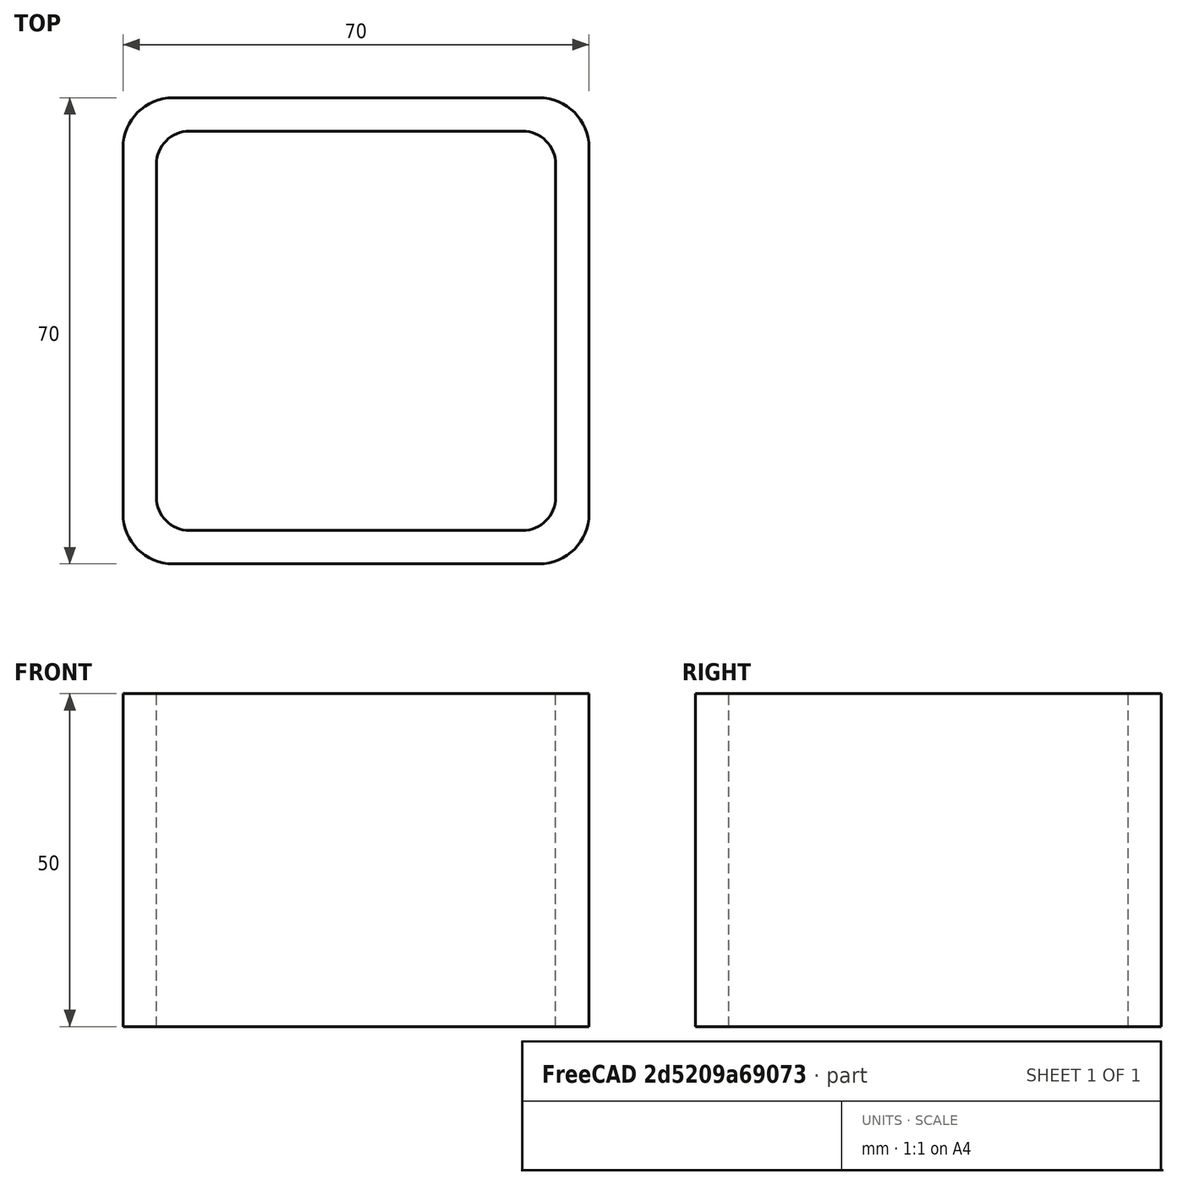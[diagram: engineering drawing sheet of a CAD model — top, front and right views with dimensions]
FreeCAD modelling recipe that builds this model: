
FCSTD DOCUMENT  (FreeCAD 0.15R4671 (Git))
Label: Square hollow section 70x70x5 EN10219 S235JRH
License: All rights reserved
LicenseURL: http://en.wikipedia.org/wiki/All_rights_reserved
objects: Sketcher::SketchObject×1, Part::Extrusion×1
note: 2 computed .brp shape members not serialized (recipe doc carries the construction recipe); baked Part::Feature solids carry a one-line shape summary decoded from their .brp

FEATURE [Sketcher::SketchObject] Sketch
  sketch-geometry (16):
    g0: LineSegment StartX=-25 StartY=30 StartZ=0 EndX=25 EndY=30 EndZ=0
    g1: LineSegment StartX=30 StartY=25 StartZ=0 EndX=30 EndY=-25 EndZ=0
    g2: LineSegment StartX=25 StartY=-30 StartZ=0 EndX=-25 EndY=-30 EndZ=0
    g3: LineSegment StartX=-30 StartY=-25 StartZ=0 EndX=-30 EndY=25 EndZ=0
    g4: LineSegment StartX=-27.5 StartY=35 StartZ=0 EndX=27.5 EndY=35 EndZ=0
    g5: LineSegment StartX=35 StartY=27.5 StartZ=0 EndX=35 EndY=-27.5 EndZ=0
    g6: LineSegment StartX=27.5 StartY=-35 StartZ=0 EndX=-27.5 EndY=-35 EndZ=0
    g7: LineSegment StartX=-35 StartY=-27.5 StartZ=0 EndX=-35 EndY=27.5 EndZ=0
    g8: ArcOfCircle CenterX=-25 CenterY=25 CenterZ=0 NormalX=0 NormalY=0 NormalZ=1 Radius=5 StartAngle=1.5708 EndAngle=3.14159
    g9: ArcOfCircle CenterX=25 CenterY=25 CenterZ=0 NormalX=0 NormalY=0 NormalZ=1 Radius=5 StartAngle=0 EndAngle=1.5708
    g10: ArcOfCircle CenterX=25 CenterY=-25 CenterZ=0 NormalX=0 NormalY=0 NormalZ=1 Radius=5 StartAngle=4.71239 EndAngle=6.28319
    g11: ArcOfCircle CenterX=-25 CenterY=-25 CenterZ=0 NormalX=0 NormalY=0 NormalZ=1 Radius=5 StartAngle=3.14159 EndAngle=4.71239
    g12: ArcOfCircle CenterX=27.5 CenterY=27.5 CenterZ=0 NormalX=0 NormalY=0 NormalZ=1 Radius=7.5 StartAngle=0 EndAngle=1.5708
    g13: ArcOfCircle CenterX=27.5 CenterY=-27.5 CenterZ=0 NormalX=0 NormalY=0 NormalZ=1 Radius=7.5 StartAngle=4.71239 EndAngle=6.28319
    g14: ArcOfCircle CenterX=-27.5 CenterY=-27.5 CenterZ=0 NormalX=0 NormalY=0 NormalZ=1 Radius=7.5 StartAngle=3.14159 EndAngle=4.71239
    g15: ArcOfCircle CenterX=-27.5 CenterY=27.5 CenterZ=0 NormalX=0 NormalY=0 NormalZ=1 Radius=7.5 StartAngle=1.5708 EndAngle=3.14159
  constraints (36):
    c: Horizontal(g2)
    c: Vertical(g3)
    c: Horizontal(g6)
    c: Vertical(g7)
    c: Tangent(g3,g8) = 1.5708
    c: Tangent(g0,g8) = 1.5708
    c: Tangent(g0,g9) = 1.5708
    c: Tangent(g1,g9) = 1.5708
    c: Tangent(g1,g10) = 1.5708
    c: Tangent(g2,g10) = 1.5708
    c: Tangent(g2,g11) = 1.5708
    c: Tangent(g3,g11) = 1.5708
    c: Tangent(g4,g12) = 1.5708
    c: Tangent(g5,g12) = 1.5708
    c: Tangent(g5,g13) = 1.5708
    c: Tangent(g6,g13) = 1.5708
    c: Tangent(g6,g14) = 1.5708
    c: Tangent(g7,g14) = 1.5708
    c: Tangent(g7,g15) = 1.5708
    c: Tangent(g4,g15) = 1.5708
    c: Equal(g9,g8)
    c: Equal(g9,g11)
    c: Equal(g9,g10)
    c: Equal(g12,g15)
    c: Equal(g12,g14)
    c: Equal(g12,g13)
    c: Symmetric(g4,g6,g-1)
    c: Symmetric(g7,g5,g-2)
    c: DistanceY(g4,g6) = -70
    c: DistanceX(g7,g5) = 70
    c: Symmetric(g3,g1,g-2)
    c: Symmetric(g0,g2,g-1)
    c: DistanceY(g0,g4) = 5
    c: DistanceX(g5,g1) = -5
    c: Radius(g9) = 5
    c: Radius(g12) = 7.5
FEATURE [Part::Extrusion] Extrude  label="Square hollow section 70x70x5 EN10219 S235JRH"
  Base = -> Sketch
  Dir = (0,0,50)
  Solid = true
